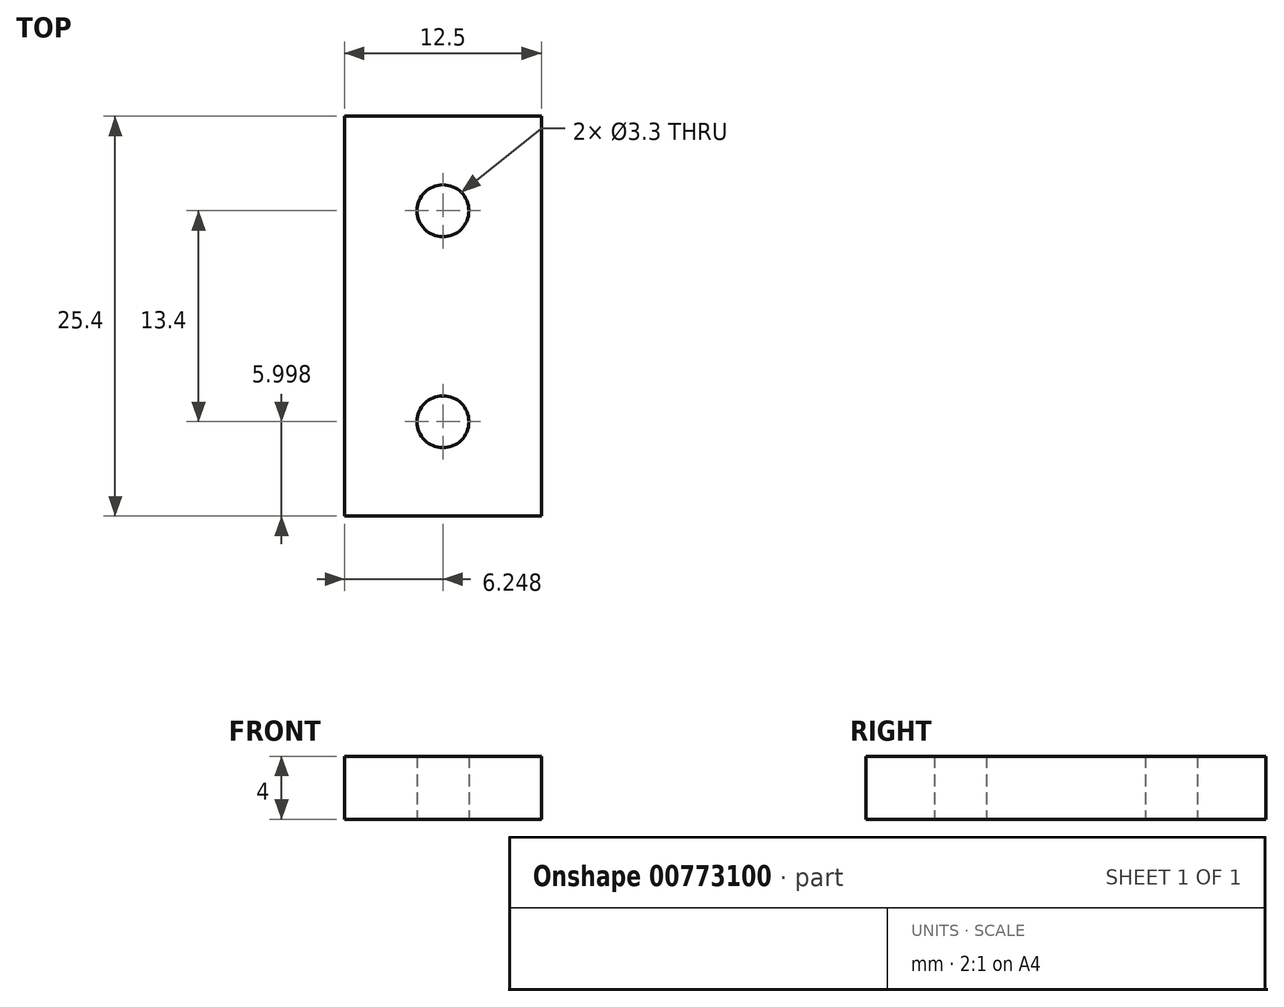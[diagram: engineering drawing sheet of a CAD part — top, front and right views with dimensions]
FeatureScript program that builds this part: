
annotation { "Feature Type Name" : "Feature", "Feature Type Description" : "" }
export const myFeature = defineFeature(function(context is Context, id is Id, definition is map)
    precondition{}
    {
        {
            var Q0;
            Q0=qCreatedBy(makeId("Top.planeOp"),FACE);
            var sketch = newSketch(context, id + "F0", { "sketchPlane" : qUnion([Q0])});
            skLineSegment(sketch, "E0.bottom", {"start": v(-4.4, 11.77) * mm, "end": v(8.1, 11.77) * mm});
            skLineSegment(sketch, "E0.top", {"start": v(-4.4, -13.63) * mm, "end": v(8.1, -13.63) * mm});
            skLineSegment(sketch, "E0.left", {"start": v(-4.4, 11.77) * mm, "end": v(-4.4, -13.63) * mm});
            skLineSegment(sketch, "E0.right", {"start": v(8.1, 11.77) * mm, "end": v(8.1, -13.63) * mm});
            skSolve(sketch);
        }
        {
            var Q0;
            Q0=makeQuery(id+"F0.imprint","IMPRINT",FACE,{"disambiguationData":[TD([[makeQuery(id+"F0.imprint","IMPRINT",EDGE,{"derivedFrom":sQuery(id+"F0.wireOp",EDGE,"E0.bottom")}),-1.0]])]});
            extrude(context, id + "F1", {"entities" : qUnion([Q0]), "depth" : 4 * mm, "offsetDistance" : 25 * mm});
        }
        {
            var Q0;
            Q0=makeQuery(id+"F1.opExtrude","CAP_FACE",FACE,{"disambiguationData":[OSD([sQuery(id+"F0.wireOp",EDGE,"E0.bottom"),sQuery(id+"F0.wireOp",EDGE,"E0.top"),sQuery(id+"F0.wireOp",EDGE,"E0.left"),sQuery(id+"F0.wireOp",EDGE,"E0.right")])],"isStart":true});
            var sketch = newSketch(context, id + "F2", { "sketchPlane" : qUnion([Q0])});
            skPoint(sketch, "E1", {"position": v(1.86, 7.63) * mm});
            skPoint(sketch, "E2", {"position": v(1.86, -5.77) * mm});
            skSolve(sketch);
        }
        {
            var Q0;
            Q0=sQuery(id+"F2.wireOp",VERTEX,"E1");
            var Q1;
            Q1=sQuery(id+"F2.wireOp",VERTEX,"E2");
            var Q2;
            Q2=makeQuery(id+"F1.opExtrude","SWEPT_BODY",BODY,{"disambiguationData":[OSD([sQuery(id+"F0.wireOp",EDGE,"E0.bottom"),sQuery(id+"F0.wireOp",EDGE,"E0.top"),sQuery(id+"F0.wireOp",EDGE,"E0.left"),sQuery(id+"F0.wireOp",EDGE,"E0.right")])]});
            hole(context, id + "F3", {"style" : HoleStyle.SIMPLE, "endStyle" : HoleEndStyle.THROUGH, "standardTappedOrClearance" : lookupTablePath({ "standard" : "ISO", "engagement" : "75%", "pitch" : "0.7 mm", "size" : "M4", "type" : "Tapped" }), "standardBlindInLast" : lookupTablePath({ "standard" : "ISO", "engagement" : "75%", "pitch" : "0.7 mm", "size" : "M4", "type" : "Tapped" }), "holeDiameter" : 3.3 * mm, "majorDiameter" : 4 * mm, "showTappedDepth" : true, "isTappedThrough" : true, "tappedDepth" : 12 * mm, "tapClearance" : 3, "locations" : qUnion([Q0, Q1]), "scope" : qUnion([Q2])});
        }
    });
